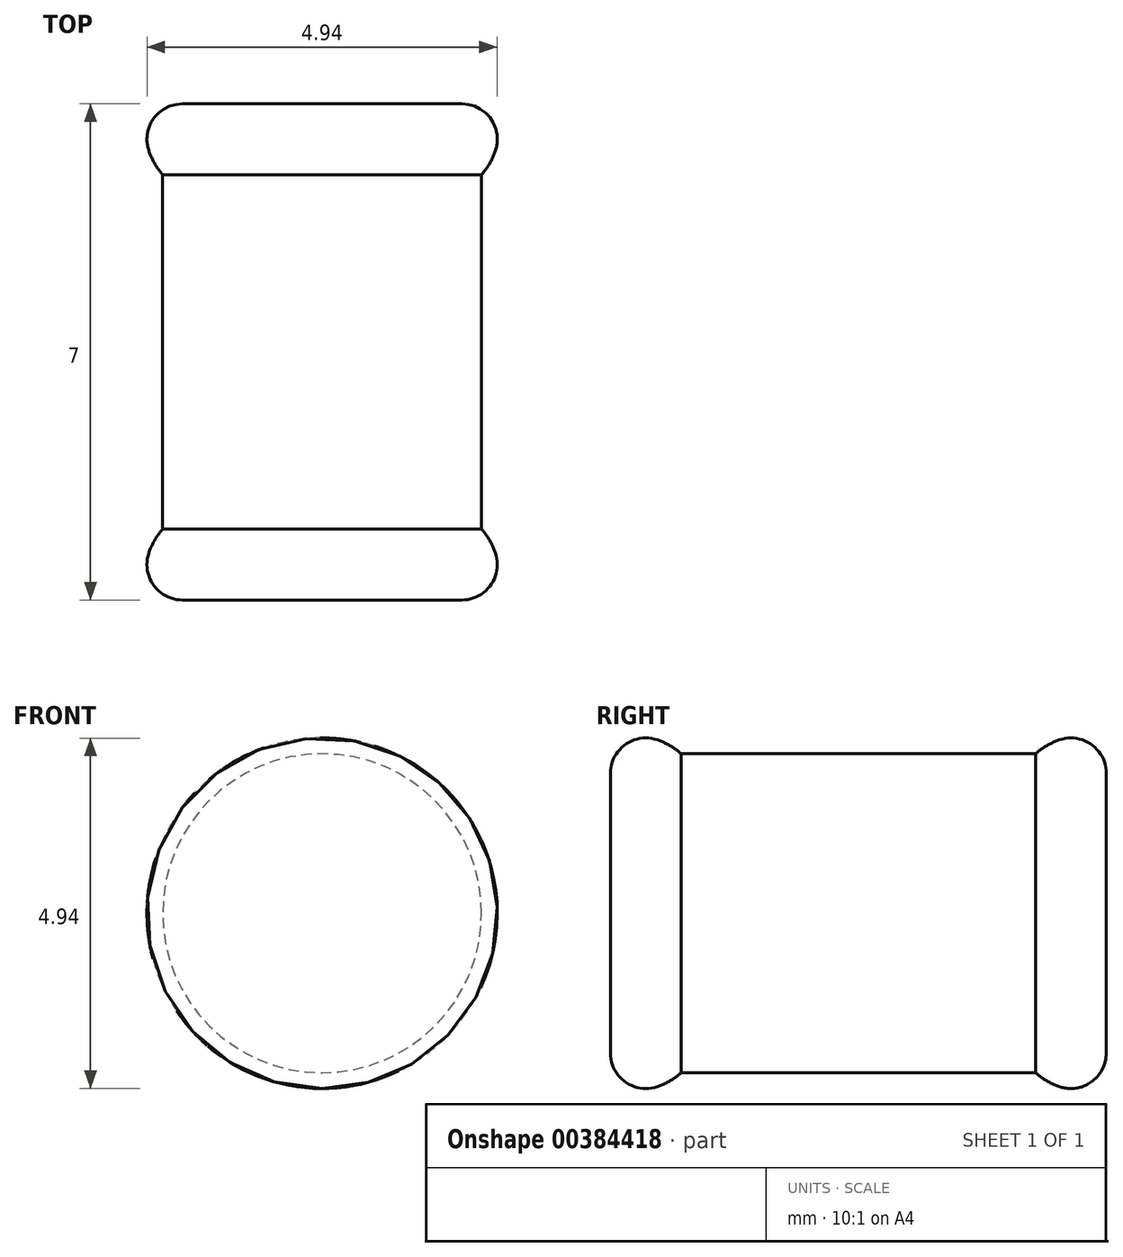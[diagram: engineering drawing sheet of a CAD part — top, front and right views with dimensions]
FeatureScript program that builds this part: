
annotation { "Feature Type Name" : "Feature", "Feature Type Description" : "" }
export const myFeature = defineFeature(function(context is Context, id is Id, definition is map)
    precondition{}
    {
        {
            var Q0;
            Q0=qCreatedBy(makeId("Front.planeOp"),FACE);
            var sketch = newSketch(context, id + "F0", { "sketchPlane" : qUnion([Q0])});
            skCircle(sketch, "E0", {"center": v(0, 0) * mm, "radius": 2.25 * mm});
            skSolve(sketch);
        }
        {
            var Q0;
            Q0 = qSketchRegion(id + "F0", true);
            extrude(context, id + "F1", {"entities" : qUnion([Q0]), "depth" : 5 * mm});
        }
        {
            var Q0;
            Q0=makeQuery(id+"F1.opExtrude","CAP_FACE",FACE,{"disambiguationData":[OSD([sQuery(id+"F0.wireOp",EDGE,"E0")])],"isStart":false});
            var sketch = newSketch(context, id + "F2", { "sketchPlane" : qUnion([Q0])});
            skCircle(sketch, "E1", {"center": v(0, 0) * mm, "radius": 2.5 * mm});
            skSolve(sketch);
        }
        {
            var Q0;
            Q0=makeQuery(id+"F2.imprint","IMPRINT",FACE,{"disambiguationData":[TD([[makeQuery(id+"F2.imprint","IMPRINT",EDGE,{"derivedFrom":sQuery(id+"F2.wireOp",EDGE,"E1")}),1.0]])]});
            var Q1;
            Q1=makeQuery(id+"F2.imprint","IMPRINT",FACE,{"disambiguationData":[TD([[makeQuery(id+"F2.imprint","IMPRINT",EDGE,{"derivedFrom":makeQuery(id+"F1.opExtrude","CAP_EDGE",EDGE,{"disambiguationData":[OSD([sQuery(id+"F0.wireOp",EDGE,"E0")])],"isStart":false})}),1.0]])]});
            extrude(context, id + "F3", {"entities" : qUnion([Q0, Q1]), "operationType" : NewBodyOperationType.ADD, "depth" : 1 * mm});
        }
        {
            var Q0;
            Q0=makeQuery(id+"F3.opExtrude","CAP_EDGE",EDGE,{"disambiguationData":[OSD([sQuery(id+"F2.wireOp",EDGE,"E1")])],"isStart":true});
            fillet(context, id + "F4", {"entities" : qUnion([Q0]), "radius" : 1 * mm, "tangentPropagation" : true, "allowEdgeOverflow" : false});
        }
        {
            var Q0;
            Q0=makeQuery(id+"F3.opExtrude","CAP_EDGE",EDGE,{"disambiguationData":[OSD([sQuery(id+"F2.wireOp",EDGE,"E1")])],"isStart":false});
            fillet(context, id + "F5", {"entities" : qUnion([Q0]), "radius" : 0.5 * mm, "tangentPropagation" : true, "allowEdgeOverflow" : false});
        }
        {
            var Q0;
            Q0=makeQuery(id+"F1.opExtrude","CAP_FACE",FACE,{"disambiguationData":[OSD([sQuery(id+"F0.wireOp",EDGE,"E0")])],"isStart":true});
            var sketch = newSketch(context, id + "F6", { "sketchPlane" : qUnion([Q0])});
            skCircle(sketch, "E2", {"center": v(0, 0) * mm, "radius": 2.5 * mm});
            skSolve(sketch);
        }
        {
            var Q0;
            Q0=makeQuery(id+"F6.imprint","IMPRINT",FACE,{"disambiguationData":[TD([[makeQuery(id+"F6.imprint","IMPRINT",EDGE,{"derivedFrom":sQuery(id+"F6.wireOp",EDGE,"E2")}),1.0]])]});
            var Q1;
            Q1=makeQuery(id+"F6.imprint","IMPRINT",FACE,{"disambiguationData":[TD([[makeQuery(id+"F6.imprint","IMPRINT",EDGE,{"derivedFrom":makeQuery(id+"F1.opExtrude","CAP_EDGE",EDGE,{"disambiguationData":[OSD([sQuery(id+"F0.wireOp",EDGE,"E0")])],"isStart":true})}),-1.0]])]});
            extrude(context, id + "F7", {"entities" : qUnion([Q0, Q1]), "operationType" : NewBodyOperationType.ADD, "depth" : 1 * mm});
        }
        {
            var Q0;
            Q0=makeQuery(id+"F7.opExtrude","CAP_EDGE",EDGE,{"disambiguationData":[OSD([sQuery(id+"F6.wireOp",EDGE,"E2")])],"isStart":true});
            fillet(context, id + "F8", {"entities" : qUnion([Q0]), "radius" : 1 * mm, "tangentPropagation" : true, "allowEdgeOverflow" : false});
        }
        {
            var Q0;
            Q0=makeQuery(id+"F7.opExtrude","CAP_EDGE",EDGE,{"disambiguationData":[OSD([sQuery(id+"F6.wireOp",EDGE,"E2")])],"isStart":false});
            fillet(context, id + "F9", {"entities" : qUnion([Q0]), "radius" : 0.5 * mm, "tangentPropagation" : true, "allowEdgeOverflow" : false});
        }
    });
